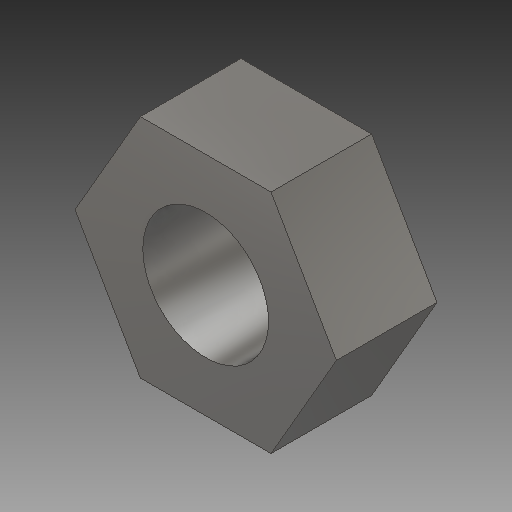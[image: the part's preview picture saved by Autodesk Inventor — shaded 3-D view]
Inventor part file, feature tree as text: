
AUTODESK INVENTOR PART (.ipt)
format: ipt  version: 2019.4 (Build 234330000, 330)  size: 110,080 bytes
history: native  units: mm
features: extrude x1, sketch x1
ambient origin geometry x8: Origin, YZ Plane, XZ Plane, XY Plane, X Axis, Y Axis, Z Axis, Center Point
bodies: Body1 (feature_tree)
feature tree (2):
  extrude  "Extrusion4"  Depth=2.4mm
  sketch  "Sketch3"  dims[d12=5.4mm d13=3.0mm d14=2.4mm d15=0.0mm]
